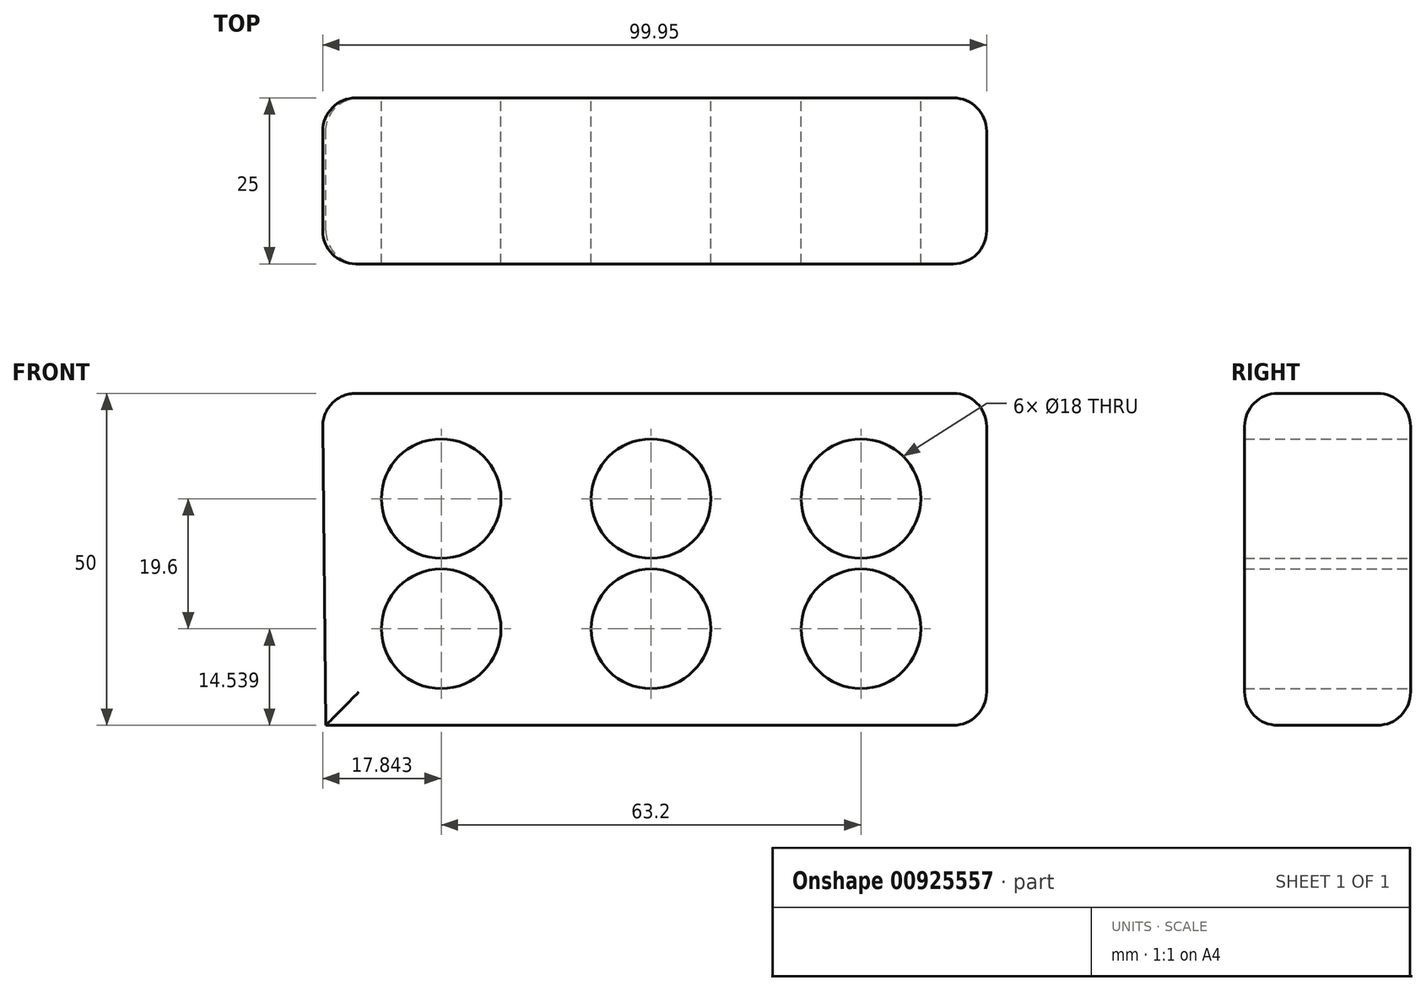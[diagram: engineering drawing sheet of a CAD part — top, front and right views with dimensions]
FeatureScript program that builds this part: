
annotation { "Feature Type Name" : "Feature", "Feature Type Description" : "" }
export const myFeature = defineFeature(function(context is Context, id is Id, definition is map)
    precondition{}
    {
        {
            var Q0;
            Q0=qCreatedBy(makeId("Front.planeOp"),FACE);
            var sketch = newSketch(context, id + "F0", { "sketchPlane" : qUnion([Q0])});
            skLineSegment(sketch, "E0", {"start": v(-53.72, 27.88) * mm, "end": v(46.28, 27.88) * mm});
            skLineSegment(sketch, "E1", {"start": v(46.28, 27.88) * mm, "end": v(46.28, -22.12) * mm});
            skLineSegment(sketch, "E2", {"start": v(46.28, -22.12) * mm, "end": v(-53.19, -22.12) * mm});
            skLineSegment(sketch, "E3", {"start": v(-53.19, -22.12) * mm, "end": v(-53.72, 27.88) * mm});
            skSolve(sketch);
        }
        {
            var Q0;
            Q0 = qSketchRegion(id + "F0", true);
            extrude(context, id + "F1", {"entities" : qUnion([Q0]), "depth" : 25 * mm, "offsetDistance" : 25 * mm});
        }
        {
            var Q0;
            Q0=makeQuery(id+"F1.opExtrude","CAP_EDGE",EDGE,{"disambiguationData":[OSD([sQuery(id+"F0.wireOp",EDGE,"E2")])],"isStart":true});
            var Q1;
            Q1=makeQuery(id+"F1.opExtrude","CAP_EDGE",EDGE,{"disambiguationData":[OSD([sQuery(id+"F0.wireOp",EDGE,"E2")])],"isStart":false});
            var Q2;
            Q2=makeQuery(id+"F1.opExtrude","CAP_FACE",FACE,{"disambiguationData":[OSD([sQuery(id+"F0.wireOp",EDGE,"E0"),sQuery(id+"F0.wireOp",EDGE,"E1"),sQuery(id+"F0.wireOp",EDGE,"E2"),sQuery(id+"F0.wireOp",EDGE,"E3")])],"isStart":false});
            var Q3;
            Q3=makeQuery(id+"F1.opExtrude","SWEPT_FACE",FACE,{"disambiguationData":[OSD([sQuery(id+"F0.wireOp",EDGE,"E0")])]});
            var Q4;
            Q4=makeQuery(id+"F1.opExtrude","CAP_FACE",FACE,{"disambiguationData":[OSD([sQuery(id+"F0.wireOp",EDGE,"E0"),sQuery(id+"F0.wireOp",EDGE,"E1"),sQuery(id+"F0.wireOp",EDGE,"E2"),sQuery(id+"F0.wireOp",EDGE,"E3")])],"isStart":true});
            var Q5;
            Q5=makeQuery(id+"F1.opExtrude","SWEPT_FACE",FACE,{"disambiguationData":[OSD([sQuery(id+"F0.wireOp",EDGE,"E1")])]});
            fillet(context, id + "F2", {"entities" : qUnion([Q0, Q1, Q2, Q3, Q4, Q5]), "radius" : 5 * mm, "tangentPropagation" : true, "allowEdgeOverflow" : false});
        }
        {
            var Q0;
            Q0=qCreatedBy(makeId("Front.planeOp"),FACE);
            var sketch = newSketch(context, id + "F3", { "sketchPlane" : qUnion([Q0])});
            skCircle(sketch, "E4", {"center": v(-35.83, 12.02) * mm, "radius": 9 * mm});
            skCircle(sketch, "E5.0.1.0", {"center": v(-35.83, -7.58) * mm, "radius": 9 * mm});
            skCircle(sketch, "E5.1.0.0", {"center": v(-4.23, 12.02) * mm, "radius": 9 * mm});
            skCircle(sketch, "E5.1.1.0", {"center": v(-4.23, -7.58) * mm, "radius": 9 * mm});
            skCircle(sketch, "E5.2.0.0", {"center": v(27.37, 12.02) * mm, "radius": 9 * mm});
            skCircle(sketch, "E5.2.1.0", {"center": v(27.37, -7.58) * mm, "radius": 9 * mm});
            skLineSegment(sketch, "E5.direction1", {"start": v(-35.83, 12.02) * mm, "end": v(-4.23, 12.02) * mm, "construction": true});
            skLineSegment(sketch, "E5.direction2", {"start": v(-35.83, 12.02) * mm, "end": v(-35.83, -7.58) * mm, "construction": true});
            skSolve(sketch);
        }
        {
            var Q0;
            Q0 = qSketchRegion(id + "F3", true);
            extrude(context, id + "F4", {"entities" : qUnion([Q0]), "operationType" : NewBodyOperationType.REMOVE, "endBound" : BoundingType.THROUGH_ALL, "depth" : 25.3 * mm, "offsetDistance" : 25 * mm});
        }
    });
